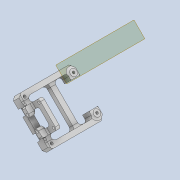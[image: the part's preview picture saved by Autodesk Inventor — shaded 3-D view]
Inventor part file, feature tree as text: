
AUTODESK INVENTOR PART (.ipt)
format: ipt  version: 2020 (Build 240168000, 168)  size: 688,640 bytes
history: native  units: mm
features: projected_geometry x18, sketch x15, thicken_offset x13, extrude x12, fillet x9, other x6, chamfer x5, hole x3, plane x1, reference x1
ambient origin geometry x8: Origin, YZ Plane, XZ Plane, XY Plane, X Axis, Y Axis, Z Axis, Center Point
bodies: Solid1 (feature_tree)
feature tree (83):
  extrude  "Extrusion1"  Depth=4.0mm
  extrude  "Extrusion2"  Depth=4.0mm
  extrude  "Extrusion3"  Depth=2.0mm
  thicken_offset  "Thicken1"
  thicken_offset  "Thicken2"
  thicken_offset  "Thicken3"
  thicken_offset  "Thicken4"
  chamfer  "Chamfer2"  Distance=6.3mm
  fillet  "Fillet5"  Radius=6.0mm
  hole  "Hole1"  [1 undecoded]
  hole  "Hole2"  [1 undecoded]
  plane  "Work Plane1"
  extrude  "Extrusion4"  Depth=0.25mm
  extrude  "Extrusion5"  Depth=0.25mm
  extrude  "Extrusion6"  Depth=1.0mm
  thicken_offset  "Thicken5"
  thicken_offset  "Thicken6"
  thicken_offset  "Thicken7"
  fillet  "Fillet8"  Radius=1.0mm
  chamfer  "Chamfer3"  Distance=2.0mm Angle=45.0deg
  fillet  "Fillet9"  Radius=2.0mm
  fillet  "Fillet10"  Radius=6.0mm
  fillet  "Fillet11"  Radius=6.0mm
  chamfer  "Chamfer4"  Distance=6.0mm
  extrude  "Extrusion7"  Depth=2.0mm
  fillet  "Fillet12"  Radius=3.5mm
  chamfer  "Chamfer5"  Distance=35.0mm
  extrude  "Extrusion8"  Depth=2.0mm
  fillet  "Fillet13"  Radius=6.3mm
  fillet  "Fillet14"  Radius=6.3mm
  extrude  "Extrusion9"  Depth=2.0mm
  extrude  "Extrusion10"  Depth=2.0mm
  extrude  "Extrusion11"  Depth=2.0mm TaperAngle=0.0deg
  sketch  "Sketch14"  dims[d44=1.9mm d45=6.0mm d46=4.0mm d47=2.0mm d48=90.0deg d49=4.0mm d50=0.0mm d51=6.0mm d52=6.0mm]
  thicken_offset  "Thicken10"
  thicken_offset  "Thicken11"
  thicken_offset  "Thicken12"
  thicken_offset  "Thicken13"
  hole  "Hole3"  [1 undecoded]
  chamfer  "Chamfer7"  Distance=1.5mm
  thicken_offset  "Thicken14"
  thicken_offset  "Thicken15"
  extrude  "Extrusion12"  Depth=2.0mm
  fillet  "Fillet15"  Radius=1.0mm
  sketch  "Sketch1"  dims[d0=4.0mm d1=4.0mm]
  reference  "Reference1"
  sketch  "Sketch2"  dims[d2=4.0mm d3=4.0mm]
  projected_geometry  "Projected Loop1"
  sketch  "Sketch3"  dims[d4=2.0mm d5=0.0mm d6=5.5mm]
  projected_geometry  "Projected Loop2"
  projected_geometry  "Projected Loop3"
  projected_geometry  "Projected Loop4"
  sketch  "Sketch4"  dims[d7=4.0mm]
  projected_geometry  "Projected Loop5"
  projected_geometry  "Projected Loop6"
  sketch  "Sketch5"  dims[d8=4.0mm]
  projected_geometry  "Projected Loop7"
  projected_geometry  "Projected Loop8"
  sketch  "Sketch6"  dims[d9=4.0mm d10=6.3mm d11=0.0mm d12=6.0mm]
  sketch  "Sketch7"  dims[d13=4.0mm d14=6.0mm]
  projected_geometry  "Projected Loop9"
  projected_geometry  "Projected Loop10"
  sketch  "Sketch8"  dims[d15=4.0mm d16=6.0mm d17=0.0mm]
  projected_geometry  "Projected Loop11"
  sketch  "Sketch9"  dims[d21=0.25mm d22=0.25mm]
  projected_geometry  "Projected Loop12"
  sketch  "Sketch10"  dims[d23=0.25mm d24=0.25mm]
  projected_geometry  "Projected Loop13"
  sketch  "Sketch11"  dims[d27=1.0mm d28=1.0mm d29=1.0mm]
  projected_geometry  "Projected Loop14"
  projected_geometry  "Projected Loop15"
  sketch  "Sketch12"  dims[d30=1.0mm d33=1.0mm d34=2.0mm d35=45.0deg d36=2.0mm]
  projected_geometry  "Projected Loop16"
  sketch  "Sketch13"  dims[d37=1.9mm d38=6.0mm d39=4.0mm d40=2.0mm d41=90.0deg d42=4.0mm d43=0.0mm]
  sketch  "Sketch15"  dims[d53=6.0mm d54=6.0mm d55=35.0mm d56=3.5mm d57=35.0mm d58=3.5mm d59=6.3mm d60=0.0mm d61=6.3mm d62=0.0mm d63=1.9mm d64=1.9mm d65=6.3mm d66=0.0mm d69=1.5mm d70=1.5mm d71=1.0mm d72=1.5mm d73=1.0mm d74=1.5mm d75=3.0mm d76=1.0mm d77=2.0mm d78=45.0deg d79=1.0mm d80=0.5mm d81=0.5mm d82=2.0mm d83=2.0mm d84=45.0deg d85=5.0mm d86=5.0mm d87=5.0mm d88=5.0mm d89=2.0mm d90=0.0mm d91=3.0mm d92=1.0mm d93=2.0mm d94=45.0deg d95=7.0mm d96=29.0mm d97=4.0mm d98=3.5mm d99=0.0mm d100=2.2mm d104=2.0mm d109=2.0mm d110=2.0mm d111=2.0mm d112=2.0mm d113=8.0mm d114=0.0mm d115=8.0mm d116=10.0mm d117=2.0mm d118=2.0mm d119=8.0mm d120=0.0mm d121=10.0mm d122=0.0mm d123=2.0mm d124=2.0mm d125=2.0mm d126=2.0mm d127=2.0mm d128=3.0mm d129=2.0mm d130=3.0mm d131=1.8mm d132=6.0mm d133=4.0mm d134=2.0mm d135=90.0deg d136=10.0mm d137=0.0mm d138=3.0mm d139=2.0mm d140=45.0deg d141=1.0mm d142=1.0mm d143=1.0mm d144=1.0mm d145=5.0mm d146=5.0mm d147=1.0mm d148=0.0mm d149=2.0mm d18=0.5mm d19=0.872665mm]
  projected_geometry  "Projected Loop17"
  projected_geometry  "Projected Loop18"
  parser-record x2  (decoder bookkeeping rows leaked as tree rows — omitted from the tree; the rows remain in map.json)
  other  "mot_27_ass.iam"
  other  "mot_27_2:1"
  other  "tip_3_ass_base.iam"
  other  "ext_shell_2:1"
note: 3 required parameter values undecoded (feature->parameter linkage not recoverable at this tier; creation-order binding heuristic only, values carry confidence <= 0.55)
note: 2 file-system paths scrubbed to <path> (originals preserved in map.json)
